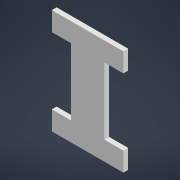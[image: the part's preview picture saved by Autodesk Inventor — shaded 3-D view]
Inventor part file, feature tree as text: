
AUTODESK INVENTOR PART (.ipt)
format: ipt  version: 2021 (Build 250183000, 183)  size: 130,048 bytes
history: native  units: mm
features: sketch x2, extrude x1
ambient origin geometry x8: Origin, YZ Plane, XZ Plane, XY Plane, X Axis, Y Axis, Z Axis, Center Point
bodies: Solid1 (feature_tree)
feature tree (3):
  extrude  "Extrusion1"  Depth=200.2mm
  sketch  "Sketch2"  dims[d2=150.0mm d3=220.2mm d4=40.0mm d5=40.0mm d6=140.2mm d7=90.0deg d8=10.0mm d9=0.0mm d10=10.0mm d11=10.0mm d12=10.0mm d13=10.0mm]
  sketch  "Sketch1"  dims[d0=130.0mm d1=200.2mm]
